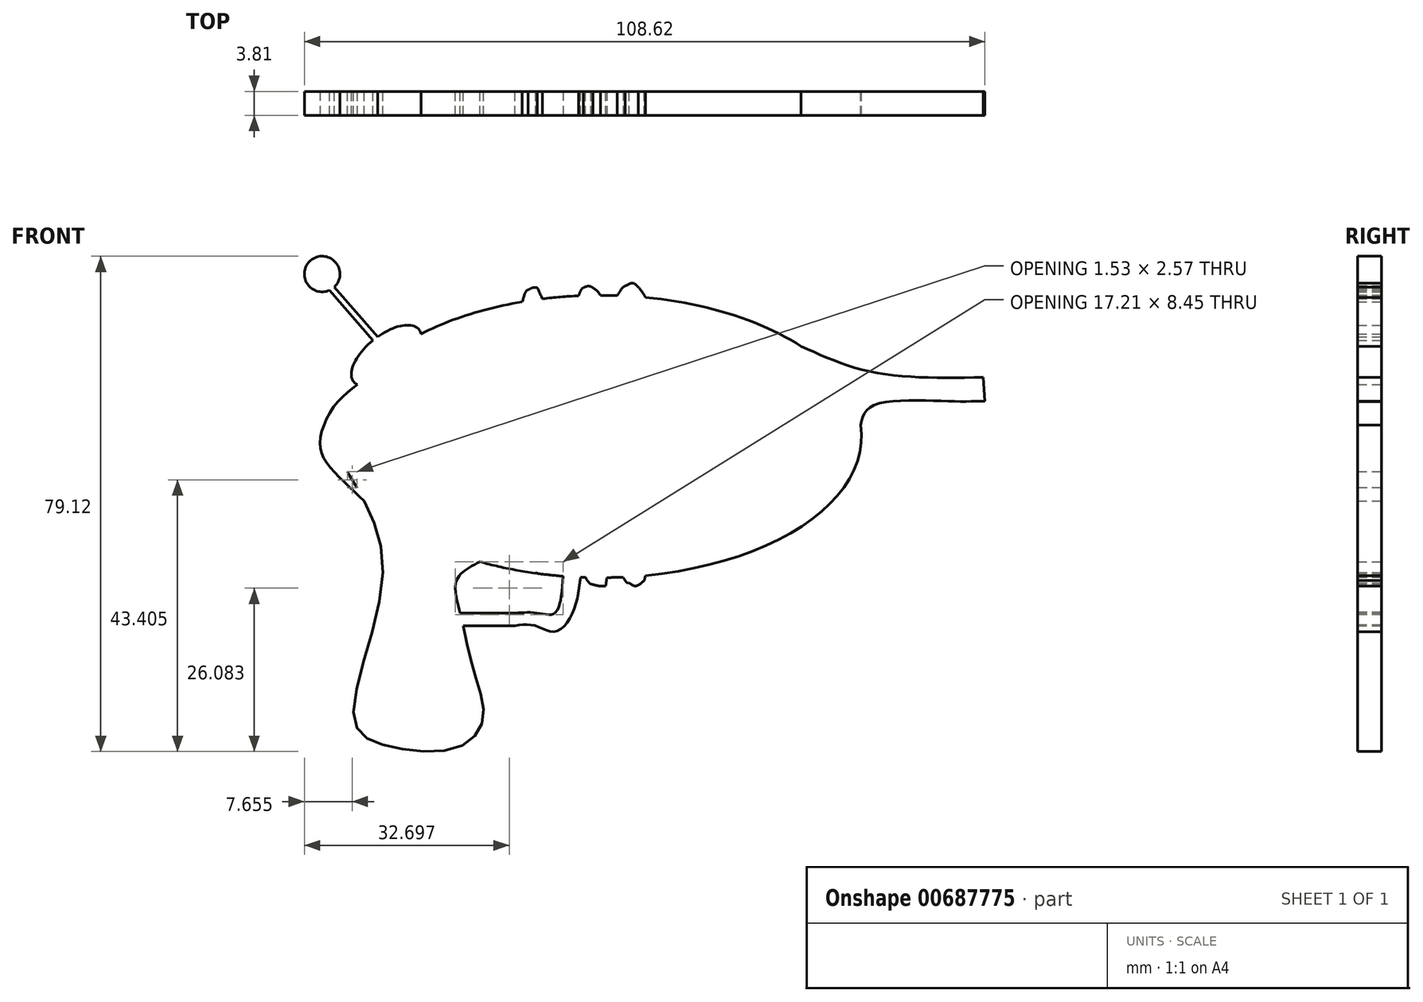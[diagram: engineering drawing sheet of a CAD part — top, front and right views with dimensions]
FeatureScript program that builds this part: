
annotation { "Feature Type Name" : "Feature", "Feature Type Description" : "" }
export const myFeature = defineFeature(function(context is Context, id is Id, definition is map)
    precondition{}
    {
        {
            var Q0;
            Q0=qCreatedBy(makeId("Front.planeOp"),FACE);
            var sketch = newSketch(context, id + "F0", { "sketchPlane" : qUnion([Q0])});
            skEllipse(sketch, "E0", {"center": v(0, 0) * mm, "majorRadius": 41.67 * mm, "minorRadius": 22.55 * mm, "majorAxis": v(1, 0)});
            skFitSpline(sketch, "E1", {"points": [v(-40.35, -5.63) * mm, v(-34.74, -22.23) * mm, v(-39.36, -44.93) * mm, v(-34.6, -49.28) * mm, v(-22.5, -49.56) * mm, v(-18.7, -44.8) * mm, v(-20.19, -37.46) * mm, v(-22.36, -28.21) * mm, v(-22.9, -22.9) * mm, v(-19.22, -20.01) * mm], "startDerivative": vector(59.42, -98.15) * mm, "endDerivative": vector(60.59, 31.88) * mm});
            skLineSegment(sketch, "E2", {"start": v(-22.36, -28.21) * mm, "end": v(-13.63, -28.21) * mm});
            skLineSegment(sketch, "E3", {"start": v(-21.9, -30.24) * mm, "end": v(-13.63, -30.24) * mm});
            skFitSpline(sketch, "E4", {"points": [v(-13.63, -28.21) * mm, v(-10, -28.21) * mm, v(-7.27, -28.21) * mm, v(-5.94, -22.32) * mm], "startDerivative": vector(11.53, 0.81) * mm, "endDerivative": vector(1.3, 18.85) * mm});
            skFitSpline(sketch, "E5", {"points": [v(-13.63, -30.24) * mm, v(-10.37, -30.24) * mm, v(-7.27, -31.2) * mm, v(-4.42, -28.21) * mm, v(-3.16, -22.49) * mm], "startDerivative": vector(14.6, 2.11) * mm, "endDerivative": vector(2.28, 19.94) * mm});
            skFitSpline(sketch, "E6", {"points": [v(-17.45, -20.48) * mm, v(-18.33, -22.78) * mm, v(-16.62, -26.55) * mm, v(-16.38, -26.55) * mm], "startDerivative": vector(-3.85, -4.93) * mm, "endDerivative": vector(1.7, 0.89) * mm});
            skFitSpline(sketch, "E7", {"points": [v(-15.93, -20.84) * mm, v(-16.13, -22.53) * mm, v(-16.38, -26.55) * mm], "startDerivative": vector(-0.55, -3.83) * mm, "endDerivative": vector(-0.36, -7.35) * mm});
            skEllipse(sketch, "E8", {"center": v(-34.16, 12.92) * mm, "majorRadius": 6.67 * mm, "minorRadius": 3.24 * mm, "majorAxis": v(0.78, 0.62)});
            skLineSegment(sketch, "E9", {"start": v(-34.16, 12.92) * mm, "end": v(-43.67, 23.88) * mm});
            skLineSegment(sketch, "E10", {"start": v(-42.45, 23.88) * mm, "end": v(-33.42, 13.47) * mm});
            skLineSegment(sketch, "E11", {"start": v(-33.42, 13.47) * mm, "end": v(-33.31, 14.26) * mm});
            skCircle(sketch, "E12", {"center": v(-44.4, 25.95) * mm, "radius": 2.84 * mm});
            skFitSpline(sketch, "E13", {"points": [v(-38.76, 8.28) * mm, v(-36.24, 3.17) * mm, v(-35.38, -4.62) * mm, v(-37.37, -10.56) * mm], "startDerivative": vector(9.01, -15.02) * mm, "endDerivative": vector(-7.85, -17.1) * mm});
            skFitSpline(sketch, "E14", {"points": [v(-37.37, -10.56) * mm, v(-41.47, -6.7) * mm, v(-44.28, -3.16) * mm, v(-44.64, 0) * mm, v(-42.45, 4.88) * mm, v(-38.76, 8.28) * mm], "startDerivative": vector(-19.21, 17.5) * mm, "endDerivative": vector(19.08, 14.48) * mm});
            skFitSpline(sketch, "E15", {"points": [v(-12.46, 21.52) * mm, v(-11.5, 23.4) * mm, v(-8.22, 10) * mm, v(-6.88, -4.75) * mm, v(-8.22, -19.85) * mm, v(-9.13, -22) * mm, v(-9.95, -21.9) * mm, v(-10.35, -21.85) * mm, v(-9.07, -23.5) * mm, v(-5.94, -19.85) * mm, v(-3.83, -4.62) * mm, v(-5.05, 10.48) * mm, v(-10.04, 23.76) * mm], "startDerivative": vector(18.77, 64.42) * mm, "endDerivative": vector(-48.51, 107.98) * mm});
            skFitSpline(sketch, "E16", {"points": [v(-11.5, 23.4) * mm, v(-10.75, 23.78) * mm, v(-10.04, 23.76) * mm], "startDerivative": vector(1.43, 0.93) * mm, "endDerivative": vector(1.5, -0.22) * mm});
            skPoint(sketch, "E17.3.internal.snap0", {"position": v(0, 22.55) * mm});
            skFitSpline(sketch, "E17", {"points": [v(-3.46, 22.47) * mm, v(-2.7, 23.76) * mm, v(-1.52, 22.54) * mm, v(0, 10.9) * mm, v(0, -4.6) * mm, v(-1.19, -22.54) * mm, v(-1.52, -23.57) * mm, v(-2.37, -22.52) * mm], "startDerivative": vector(8.42, 24.9) * mm, "endDerivative": vector(-13.5, 22.51) * mm});
            skFitSpline(sketch, "E18", {"points": [v(-1.18, 23.76) * mm, v(0, 22.55) * mm, v(2.46, 11.31) * mm, v(3.05, -4.62) * mm, v(0.85, -23.9) * mm], "startDerivative": vector(12.07, -7.71) * mm, "endDerivative": vector(-8.38, -58.92) * mm});
            skFitSpline(sketch, "E19", {"points": [v(-1.52, -23.57) * mm, v(0, -23.9) * mm, v(0.85, -23.9) * mm], "startDerivative": vector(2.83, -0.76) * mm, "endDerivative": vector(1.86, 0.12) * mm});
            skFitSpline(sketch, "E20", {"points": [v(-2.7, 23.76) * mm, v(-1.83, 24.03) * mm, v(-1.18, 23.76) * mm], "startDerivative": vector(1.7, 0.8) * mm, "endDerivative": vector(1.34, -0.82) * mm});
            skFitSpline(sketch, "E21", {"points": [v(2.72, 22.5) * mm, v(4, 24.03) * mm, v(5.16, 22.38) * mm, v(8.48, 10.18) * mm, v(7.67, -6.72) * mm, v(4.57, -23.4) * mm, v(3.64, -22.47) * mm], "startDerivative": vector(14.73, 25.68) * mm, "endDerivative": vector(-12.6, 23.08) * mm});
            skFitSpline(sketch, "E22", {"points": [v(6.06, 23.86) * mm, v(7.22, 22.21) * mm, v(10.78, 10.53) * mm, v(10.32, -7.18) * mm, v(6.98, -23.03) * mm], "startDerivative": vector(9.74, -11.4) * mm, "endDerivative": vector(-12.16, -50.74) * mm});
            skFitSpline(sketch, "E23", {"points": [v(4.57, -23.4) * mm, v(5.66, -23.87) * mm, v(6.98, -23.03) * mm], "startDerivative": vector(2.3, -1.63) * mm, "endDerivative": vector(2.51, 2.28) * mm});
            skFitSpline(sketch, "E24", {"points": [v(4, 24.03) * mm, v(5.16, 24.48) * mm, v(6.06, 23.86) * mm], "startDerivative": vector(2.34, 1.28) * mm, "endDerivative": vector(1.8, -1.65) * mm});
            skFitSpline(sketch, "E25", {"points": [v(32.03, 14.42) * mm, v(43.57, 10.26) * mm, v(61.11, 9.45) * mm], "startDerivative": vector(23.83, -10.8) * mm, "endDerivative": vector(34.06, 0.57) * mm});
            skFitSpline(sketch, "E26", {"points": [v(41.53, 1.84) * mm, v(43.3, 4.83) * mm, v(55.13, 5.64) * mm, v(61.38, 5.64) * mm], "startDerivative": vector(3.27, 14.5) * mm, "endDerivative": vector(16.38, 0.37) * mm});
            skLineSegment(sketch, "E27", {"start": v(61.11, 9.45) * mm, "end": v(61.38, 5.64) * mm});
            skSolve(sketch);
        }
        {
            var Q0;
            Q0=qSketchRegion(id+"F0",true);
            extrude(context, id + "F1", {"entities" : qUnion([Q0]), "depth" : 3.8 * mm});
        }
    });
